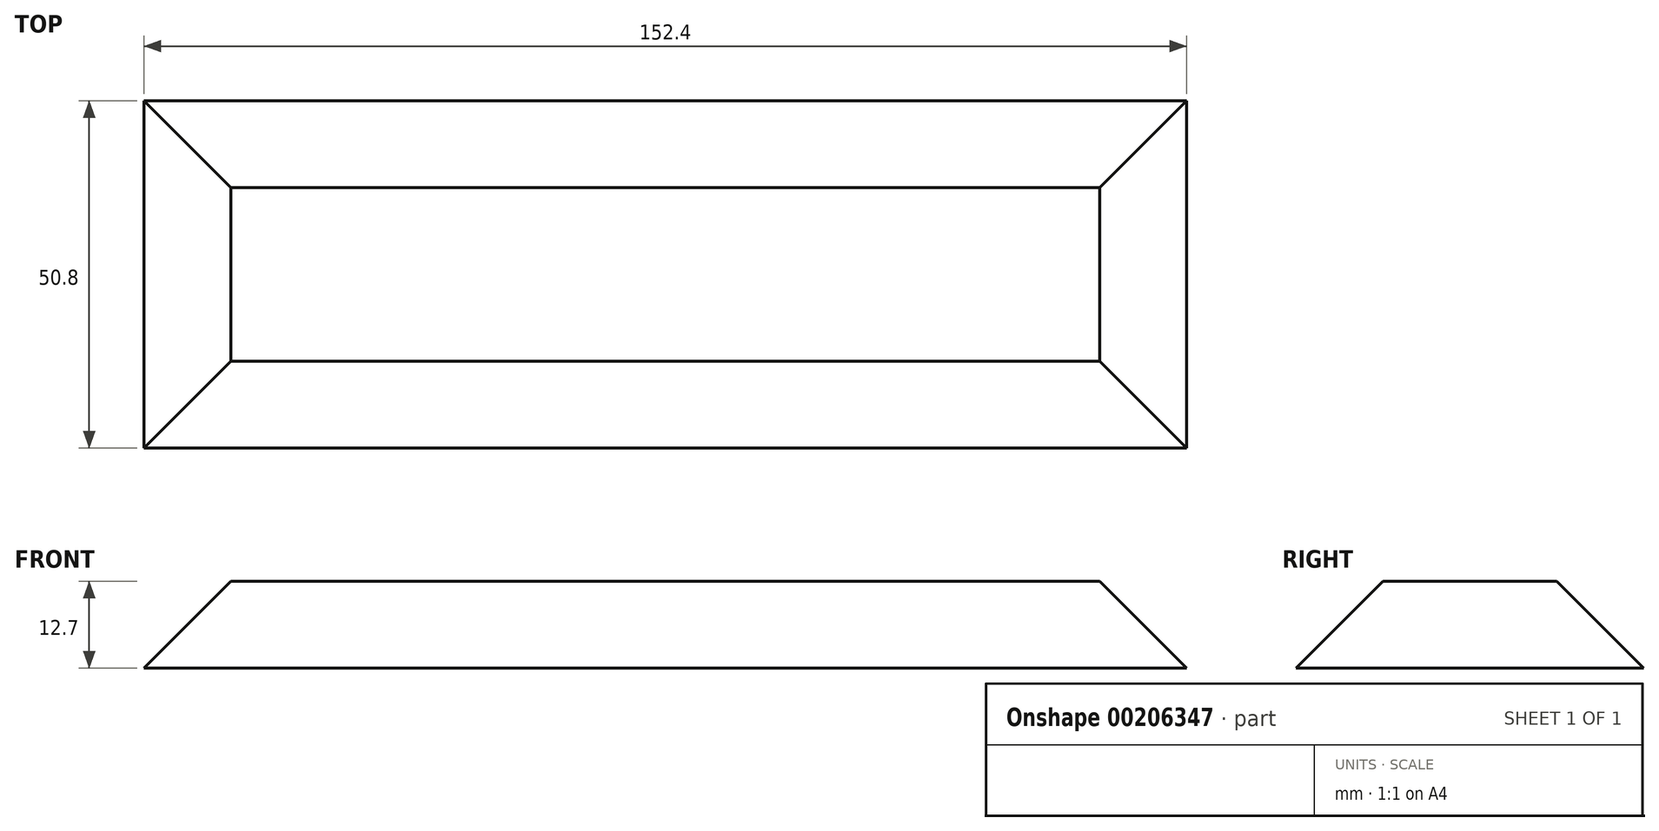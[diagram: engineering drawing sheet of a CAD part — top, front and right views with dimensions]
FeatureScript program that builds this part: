
annotation { "Feature Type Name" : "Feature", "Feature Type Description" : "" }
export const myFeature = defineFeature(function(context is Context, id is Id, definition is map)
    precondition{}
    {
        {
            var Q0;
            Q0=qCreatedBy(makeId("Right.planeOp"),FACE);
            var sketch = newSketch(context, id + "F0", { "sketchPlane" : qUnion([Q0])});
            skLineSegment(sketch, "E0.bottom", {"start": v(25.4, 6.35) * mm, "end": v(-25.4, 6.35) * mm});
            skLineSegment(sketch, "E0.top", {"start": v(25.4, -6.35) * mm, "end": v(-25.4, -6.35) * mm});
            skLineSegment(sketch, "E0.left", {"start": v(25.4, 6.35) * mm, "end": v(25.4, -6.35) * mm});
            skLineSegment(sketch, "E0.right", {"start": v(-25.4, 6.35) * mm, "end": v(-25.4, -6.35) * mm});
            skPoint(sketch, "E0.middle", {"position": v(0, 0) * mm});
            skSolve(sketch);
        }
        {
            var Q0;
            Q0=makeQuery(id+"F0.imprint","IMPRINT",FACE,{"disambiguationData":[TD([[makeQuery(id+"F0.imprint","IMPRINT",EDGE,{"derivedFrom":sQuery(id+"F0.wireOp",EDGE,"E0.bottom")}),1.0]])]});
            extrude(context, id + "F1", {"entities" : qUnion([Q0]), "endBound" : BoundingType.SYMMETRIC, "depth" : 152.4 * mm});
        }
        {
            var Q0;
            Q0=makeQuery(id+"F1.opExtrude","SWEPT_FACE",FACE,{"disambiguationData":[OSD([sQuery(id+"F0.wireOp",EDGE,"E0.bottom")])]});
            chamfer(context, id + "F2", {"entities" : qUnion([Q0]), "width" : 12.7 * mm, "tangentPropagation" : true});
        }
    });
